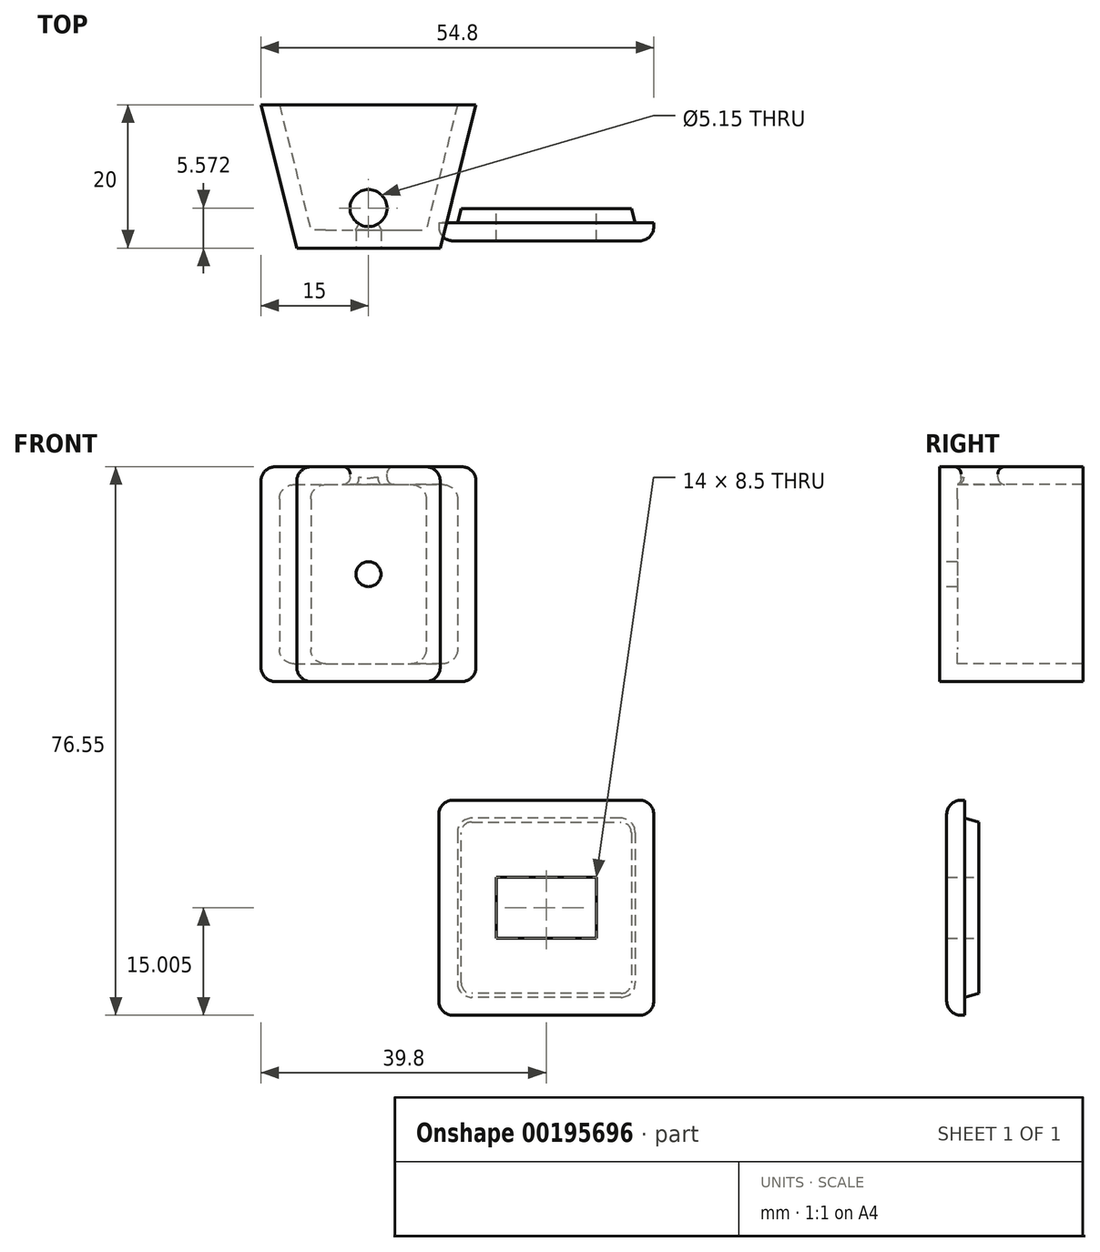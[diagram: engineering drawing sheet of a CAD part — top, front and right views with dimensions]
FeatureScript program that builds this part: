
annotation { "Feature Type Name" : "Feature", "Feature Type Description" : "" }
export const myFeature = defineFeature(function(context is Context, id is Id, definition is map)
    precondition{}
    {
        {
            var Q0;
            Q0=qCreatedBy(makeId("Top.planeOp"),FACE);
            var sketch = newSketch(context, id + "F0", { "sketchPlane" : qUnion([Q0])});
            skLineSegment(sketch, "E0.bottom", {"start": v(-10, 10) * mm, "end": v(10, 10) * mm});
            skLineSegment(sketch, "E0.top", {"start": v(-10, -10) * mm, "end": v(10, -10) * mm});
            skLineSegment(sketch, "E1", {"start": v(-15, 10) * mm, "end": v(15, 10) * mm});
            skLineSegment(sketch, "E2", {"start": v(15, 10) * mm, "end": v(10, -10) * mm});
            skLineSegment(sketch, "E3", {"start": v(-15, 10) * mm, "end": v(-10, -10) * mm});
            skSolve(sketch);
        }
        {
            var Q0;
            Q0=makeQuery(id+"F0.imprint","IMPRINT",FACE,{"disambiguationData":[TD([[makeQuery(id+"F0.imprint","IMPRINT",EDGE,{"derivedFrom":sQuery(id+"F0.wireOp",EDGE,"E0.top")}),1.0]])]});
            extrude(context, id + "F1", {"entities" : qUnion([Q0]), "depth" : 30 * mm});
        }
        {
            var Q0;
            Q0=makeQuery(id+"F1.opExtrude","SWEPT_FACE",FACE,{"disambiguationData":[OSD([sQuery(id+"F0.wireOp",EDGE,"E1")])]});
            shell(context, id + "F2", {"entities" : qUnion([Q0]), "thickness" : 2.5 * mm});
        }
        {
            var Q0;
            Q0=makeQuery(id+"F1.opExtrude","CAP_EDGE",EDGE,{"disambiguationData":[OSD([sQuery(id+"F0.wireOp",EDGE,"E3")])],"isStart":true});
            var Q1;
            Q1=makeQuery(id+"F1.opExtrude","CAP_EDGE",EDGE,{"disambiguationData":[OSD([sQuery(id+"F0.wireOp",EDGE,"E3")])],"isStart":false});
            var Q2;
            Q2=makeQuery(id+"F1.opExtrude","CAP_EDGE",EDGE,{"disambiguationData":[OSD([sQuery(id+"F0.wireOp",EDGE,"E2")])],"isStart":false});
            var Q3;
            Q3=makeQuery(id+"F1.opExtrude","CAP_EDGE",EDGE,{"disambiguationData":[OSD([sQuery(id+"F0.wireOp",EDGE,"E2")])],"isStart":true});
            var Q4;
            {var subQ0=sQuery(id+"F0.wireOp",EDGE,"E3");Q4=makeQuery(id+"F2.opShell","OFFSET_EDGE",EDGE,{"disambiguationData":[OSD([subQ0]),TDD([makeQuery(id+"F1.opExtrude","CAP_EDGE",EDGE,{"disambiguationData":[OSD([subQ0])],"isStart":false})])]});}
            var Q5;
            {var subQ0=sQuery(id+"F0.wireOp",EDGE,"E2");Q5=makeQuery(id+"F2.opShell","OFFSET_EDGE",EDGE,{"disambiguationData":[OSD([subQ0]),TDD([makeQuery(id+"F1.opExtrude","CAP_EDGE",EDGE,{"disambiguationData":[OSD([subQ0])],"isStart":false})])]});}
            var Q6;
            {var subQ0=sQuery(id+"F0.wireOp",EDGE,"E2");Q6=makeQuery(id+"F2.opShell","OFFSET_EDGE",EDGE,{"disambiguationData":[OSD([subQ0]),TDD([makeQuery(id+"F1.opExtrude","CAP_EDGE",EDGE,{"disambiguationData":[OSD([subQ0])],"isStart":true})])]});}
            var Q7;
            {var subQ0=sQuery(id+"F0.wireOp",EDGE,"E3");Q7=makeQuery(id+"F2.opShell","OFFSET_EDGE",EDGE,{"disambiguationData":[OSD([subQ0]),TDD([makeQuery(id+"F1.opExtrude","CAP_EDGE",EDGE,{"disambiguationData":[OSD([subQ0])],"isStart":true})])]});}
            fillet(context, id + "F3", {"entities" : qUnion([Q0, Q1, Q2, Q3, Q4, Q5, Q6, Q7]), "radius" : 2 * mm, "tangentPropagation" : true, "allowEdgeOverflow" : false});
        }
        {
            var Q0;
            Q0=qCreatedBy(makeId("Front.planeOp"),FACE);
            var sketch = newSketch(context, id + "F4", { "sketchPlane" : qUnion([Q0])});
            skLineSegment(sketch, "E4.bottom", {"start": v(15, -46.55) * mm, "end": v(-15, -46.55) * mm});
            skLineSegment(sketch, "E4.top", {"start": v(15, -16.55) * mm, "end": v(-15, -16.55) * mm});
            skLineSegment(sketch, "E4.left", {"start": v(15, -46.55) * mm, "end": v(15, -16.55) * mm});
            skLineSegment(sketch, "E4.right", {"start": v(-15, -46.55) * mm, "end": v(-15, -16.55) * mm});
            skLineSegment(sketch, "E5.bottom", {"start": v(12.4, -44.05) * mm, "end": v(-12.4, -44.05) * mm});
            skLineSegment(sketch, "E5.top", {"start": v(12.4, -19.05) * mm, "end": v(-12.4, -19.05) * mm});
            skLineSegment(sketch, "E5.left", {"start": v(12.4, -44.05) * mm, "end": v(12.4, -19.05) * mm});
            skLineSegment(sketch, "E5.right", {"start": v(-12.4, -44.05) * mm, "end": v(-12.4, -19.05) * mm});
            skSolve(sketch);
        }
        {
            var Q0;
            Q0=makeQuery(id+"F4.imprint","IMPRINT",FACE,{"disambiguationData":[TD([[makeQuery(id+"F4.imprint","IMPRINT",EDGE,{"derivedFrom":sQuery(id+"F4.wireOp",EDGE,"E4.bottom")}),-1.0]])]});
            var Q1;
            Q1=makeQuery(id+"F4.imprint","IMPRINT",FACE,{"disambiguationData":[TD([[makeQuery(id+"F4.imprint","IMPRINT",EDGE,{"derivedFrom":sQuery(id+"F4.wireOp",EDGE,"E5.bottom")}),-1.0]])]});
            extrude(context, id + "F5", {"entities" : qUnion([Q0, Q1]), "depth" : 2.5 * mm});
        }
        {
            var Q0;
            Q0=makeQuery(id+"F4.imprint","IMPRINT",FACE,{"disambiguationData":[TD([[makeQuery(id+"F4.imprint","IMPRINT",EDGE,{"derivedFrom":sQuery(id+"F4.wireOp",EDGE,"E5.bottom")}),-1.0]])]});
            extrude(context, id + "F6", {"entities" : qUnion([Q0]), "operationType" : NewBodyOperationType.ADD, "depth" : 4.5 * mm});
        }
        {
            var Q0;
            Q0=makeQuery(id+"F5.opExtrude","SWEPT_EDGE",EDGE,{"disambiguationData":[OSD([sQuery(id+"F4.wireOp",EDGE,"E4.bottom"),sQuery(id+"F4.wireOp",EDGE,"E4.left")])]});
            var Q1;
            Q1=makeQuery(id+"F6.opExtrude","SWEPT_EDGE",EDGE,{"disambiguationData":[OSD([sQuery(id+"F4.wireOp",EDGE,"E5.bottom"),sQuery(id+"F4.wireOp",EDGE,"E5.left")])]});
            var Q2;
            Q2=makeQuery(id+"F5.opExtrude","SWEPT_EDGE",EDGE,{"disambiguationData":[OSD([sQuery(id+"F4.wireOp",EDGE,"E4.top"),sQuery(id+"F4.wireOp",EDGE,"E4.left")])]});
            var Q3;
            Q3=makeQuery(id+"F6.opExtrude","SWEPT_EDGE",EDGE,{"disambiguationData":[OSD([sQuery(id+"F4.wireOp",EDGE,"E5.top"),sQuery(id+"F4.wireOp",EDGE,"E5.left")])]});
            var Q4;
            Q4=makeQuery(id+"F5.opExtrude","SWEPT_EDGE",EDGE,{"disambiguationData":[OSD([sQuery(id+"F4.wireOp",EDGE,"E4.bottom"),sQuery(id+"F4.wireOp",EDGE,"E4.right")])]});
            var Q5;
            Q5=makeQuery(id+"F6.opExtrude","SWEPT_EDGE",EDGE,{"disambiguationData":[OSD([sQuery(id+"F4.wireOp",EDGE,"E5.bottom"),sQuery(id+"F4.wireOp",EDGE,"E5.right")])]});
            var Q6;
            Q6=makeQuery(id+"F6.opExtrude","SWEPT_EDGE",EDGE,{"disambiguationData":[OSD([sQuery(id+"F4.wireOp",EDGE,"E5.top"),sQuery(id+"F4.wireOp",EDGE,"E5.right")])]});
            var Q7;
            Q7=makeQuery(id+"F5.opExtrude","SWEPT_EDGE",EDGE,{"disambiguationData":[OSD([sQuery(id+"F4.wireOp",EDGE,"E4.top"),sQuery(id+"F4.wireOp",EDGE,"E4.right")])]});
            fillet(context, id + "F7", {"entities" : qUnion([Q0, Q1, Q2, Q3, Q4, Q5, Q6, Q7]), "radius" : 2 * mm, "tangentPropagation" : true, "allowEdgeOverflow" : false});
        }
        {
            var Q0;
            Q0=makeQuery(id+"F5.opExtrude","CAP_FACE",FACE,{"disambiguationData":[OSD([sQuery(id+"F4.wireOp",EDGE,"E4.bottom"),sQuery(id+"F4.wireOp",EDGE,"E4.top"),sQuery(id+"F4.wireOp",EDGE,"E4.left"),sQuery(id+"F4.wireOp",EDGE,"E4.right")])],"isStart":true});
            fillet(context, id + "F8", {"entities" : qUnion([Q0]), "radius" : 2 * mm, "tangentPropagation" : true, "allowEdgeOverflow" : false});
        }
        {
            var Q0;
            Q0=makeQuery(id+"F5.opExtrude","SWEPT_BODY",BODY,{"disambiguationData":[OSD([sQuery(id+"F4.wireOp",EDGE,"E4.bottom"),sQuery(id+"F4.wireOp",EDGE,"E4.top"),sQuery(id+"F4.wireOp",EDGE,"E4.left"),sQuery(id+"F4.wireOp",EDGE,"E4.right")])]});
            var Q1;
            Q1=makeQuery(id+"F6.opExtrude","CAP_EDGE",EDGE,{"disambiguationData":[OSD([sQuery(id+"F4.wireOp",EDGE,"E5.left")])],"isStart":false});
            transform(context, id + "F9", {"entities" : qUnion([Q0]), "transformType" : TransformType.ROTATION, "transformAxis" : qUnion([Q1]), "angle" : 180 * degree, "makeCopy" : false});
        }
        {
            var Q0;
            Q0=makeQuery(id+"F6.opExtrude","CAP_FACE",FACE,{"disambiguationData":[OSD([sQuery(id+"F4.wireOp",EDGE,"E5.bottom"),sQuery(id+"F4.wireOp",EDGE,"E5.top"),sQuery(id+"F4.wireOp",EDGE,"E5.left"),sQuery(id+"F4.wireOp",EDGE,"E5.right")])],"isStart":false});
            var sketch = newSketch(context, id + "F10", { "sketchPlane" : qUnion([Q0])});
            skLineSegment(sketch, "E6", {"start": v(-24.8, -10.4) * mm, "end": v(-24.8, -54.16) * mm, "construction": true});
            skPoint(sketch, "E6.startSnap0", {"position": v(-24.8, -19.05) * mm});
            skLineSegment(sketch, "E7", {"start": v(-5.09, -31.55) * mm, "end": v(-53.1, -31.55) * mm, "construction": true});
            skPoint(sketch, "E7.startSnap0", {"position": v(-12.4, -31.55) * mm});
            skPoint(sketch, "E7.endSnap0", {"position": v(-37.2, -31.55) * mm});
            skLineSegment(sketch, "E8.bottom", {"start": v(-17.8, -27.3) * mm, "end": v(-31.8, -27.3) * mm});
            skLineSegment(sketch, "E8.top", {"start": v(-17.8, -35.8) * mm, "end": v(-31.8, -35.8) * mm});
            skLineSegment(sketch, "E8.left", {"start": v(-17.8, -27.3) * mm, "end": v(-17.8, -35.8) * mm});
            skLineSegment(sketch, "E8.right", {"start": v(-31.8, -27.3) * mm, "end": v(-31.8, -35.8) * mm});
            skSolve(sketch);
        }
        {
            var Q0;
            Q0 = qSketchRegion(id + "F10", true);
            extrude(context, id + "F11", {"entities" : qUnion([Q0]), "operationType" : NewBodyOperationType.REMOVE, "oppositeDirection" : true, "depth" : 5 * mm});
        }
        {
            var Q0;
            Q0=makeQuery(id+"F1.opExtrude","CAP_FACE",FACE,{"disambiguationData":[OSD([sQuery(id+"F0.wireOp",EDGE,"E0.top"),sQuery(id+"F0.wireOp",EDGE,"E1"),sQuery(id+"F0.wireOp",EDGE,"E2"),sQuery(id+"F0.wireOp",EDGE,"E3")])],"isStart":false});
            var sketch = newSketch(context, id + "F12", { "sketchPlane" : qUnion([Q0])});
            skCircle(sketch, "E9", {"center": v(0, -4.43) * mm, "radius": 2.57 * mm});
            skPoint(sketch, "E9.centerSnap0", {"position": v(-7.28, -4.43) * mm});
            skSolve(sketch);
        }
        {
            var Q0;
            Q0=makeQuery(id+"F12.imprint","IMPRINT",FACE,{"disambiguationData":[TD([[makeQuery(id+"F12.imprint","IMPRINT",EDGE,{"derivedFrom":sQuery(id+"F12.wireOp",EDGE,"E9")}),1.0]])]});
            extrude(context, id + "F13", {"entities" : qUnion([Q0]), "operationType" : NewBodyOperationType.REMOVE, "oppositeDirection" : true, "depth" : 5 * mm});
        }
        {
            var Q0;
            Q0=makeQuery(id+"F13.boolean.opBoolean","COPY",EDGE,{"derivedFrom":makeQuery(id+"F13.opExtrude","CAP_EDGE",EDGE,{"disambiguationData":[OSD([sQuery(id+"F12.wireOp",EDGE,"E9")])],"isStart":true})});
            var Q1;
            Q1=makeQuery(id+"F13.boolean.opBoolean","COPY",FACE,{"derivedFrom":makeQuery(id+"F13.opExtrude","SWEPT_FACE",FACE,{"disambiguationData":[OSD([sQuery(id+"F12.wireOp",EDGE,"E9")])]})});
            fillet(context, id + "F14", {"entities" : qUnion([Q0, Q1]), "radius" : 1 * mm, "tangentPropagation" : true, "allowEdgeOverflow" : false});
        }
        {
            var Q0;
            Q0=makeQuery(id+"F6.opExtrude","CAP_EDGE",EDGE,{"disambiguationData":[OSD([sQuery(id+"F4.wireOp",EDGE,"E5.right")])],"isStart":false});
            var Q1;
            Q1=makeQuery(id+"F6.opExtrude","CAP_EDGE",EDGE,{"disambiguationData":[OSD([sQuery(id+"F4.wireOp",EDGE,"E5.top")])],"isStart":false});
            var Q2;
            Q2=makeQuery(id+"F6.opExtrude","CAP_EDGE",EDGE,{"disambiguationData":[OSD([sQuery(id+"F4.wireOp",EDGE,"E5.left")])],"isStart":false});
            var Q3;
            Q3=makeQuery(id+"F6.opExtrude","CAP_EDGE",EDGE,{"disambiguationData":[OSD([sQuery(id+"F4.wireOp",EDGE,"E5.bottom")])],"isStart":false});
            var Q4;
            {var subQ0=sQuery(id+"F4.wireOp",EDGE,"E5.right");var subQ1=sQuery(id+"F4.wireOp",EDGE,"E5.top");Q4=makeQuery(id+"F7.opFillet","BLEND_EDGE",EDGE,{"blendedFrom":[makeQuery(id+"F6.opExtrude","SWEPT_EDGE",EDGE,{"disambiguationData":[OSD([subQ1,subQ0])]}),makeQuery(id+"F6.opExtrude","CAP_FACE",FACE,{"disambiguationData":[OSD([sQuery(id+"F4.wireOp",EDGE,"E5.bottom"),subQ1,sQuery(id+"F4.wireOp",EDGE,"E5.left"),subQ0])],"isStart":false})],"blendedInto":[makeQuery(id+"F6.opExtrude","CAP_FACE",FACE,{"disambiguationData":[OSD([sQuery(id+"F4.wireOp",EDGE,"E5.bottom"),subQ1,sQuery(id+"F4.wireOp",EDGE,"E5.left"),subQ0])],"isStart":false})]});}
            var Q5;
            {var subQ0=sQuery(id+"F4.wireOp",EDGE,"E5.right");var subQ1=sQuery(id+"F4.wireOp",EDGE,"E5.bottom");Q5=makeQuery(id+"F7.opFillet","BLEND_EDGE",EDGE,{"blendedFrom":[makeQuery(id+"F6.opExtrude","SWEPT_EDGE",EDGE,{"disambiguationData":[OSD([subQ1,subQ0])]}),makeQuery(id+"F6.opExtrude","CAP_FACE",FACE,{"disambiguationData":[OSD([subQ1,sQuery(id+"F4.wireOp",EDGE,"E5.top"),sQuery(id+"F4.wireOp",EDGE,"E5.left"),subQ0])],"isStart":false})],"blendedInto":[makeQuery(id+"F6.opExtrude","CAP_FACE",FACE,{"disambiguationData":[OSD([subQ1,sQuery(id+"F4.wireOp",EDGE,"E5.top"),sQuery(id+"F4.wireOp",EDGE,"E5.left"),subQ0])],"isStart":false})]});}
            var Q6;
            {var subQ0=sQuery(id+"F4.wireOp",EDGE,"E5.left");var subQ1=sQuery(id+"F4.wireOp",EDGE,"E5.top");Q6=makeQuery(id+"F7.opFillet","BLEND_EDGE",EDGE,{"blendedFrom":[makeQuery(id+"F6.opExtrude","SWEPT_EDGE",EDGE,{"disambiguationData":[OSD([subQ1,subQ0])]}),makeQuery(id+"F6.opExtrude","CAP_FACE",FACE,{"disambiguationData":[OSD([sQuery(id+"F4.wireOp",EDGE,"E5.bottom"),subQ1,subQ0,sQuery(id+"F4.wireOp",EDGE,"E5.right")])],"isStart":false})],"blendedInto":[makeQuery(id+"F6.opExtrude","CAP_FACE",FACE,{"disambiguationData":[OSD([sQuery(id+"F4.wireOp",EDGE,"E5.bottom"),subQ1,subQ0,sQuery(id+"F4.wireOp",EDGE,"E5.right")])],"isStart":false})]});}
            var Q7;
            {var subQ0=sQuery(id+"F4.wireOp",EDGE,"E5.left");var subQ1=sQuery(id+"F4.wireOp",EDGE,"E5.bottom");Q7=makeQuery(id+"F7.opFillet","BLEND_EDGE",EDGE,{"blendedFrom":[makeQuery(id+"F6.opExtrude","SWEPT_EDGE",EDGE,{"disambiguationData":[OSD([subQ1,subQ0])]}),makeQuery(id+"F6.opExtrude","CAP_FACE",FACE,{"disambiguationData":[OSD([subQ1,sQuery(id+"F4.wireOp",EDGE,"E5.top"),subQ0,sQuery(id+"F4.wireOp",EDGE,"E5.right")])],"isStart":false})],"blendedInto":[makeQuery(id+"F6.opExtrude","CAP_FACE",FACE,{"disambiguationData":[OSD([subQ1,sQuery(id+"F4.wireOp",EDGE,"E5.top"),subQ0,sQuery(id+"F4.wireOp",EDGE,"E5.right")])],"isStart":false})]});}
            chamfer(context, id + "F15", {"entities" : qUnion([Q0, Q1, Q2, Q3, Q4, Q5, Q6, Q7]), "chamferType" : ChamferType.OFFSET_ANGLE, "width" : 2 * mm, "oppositeDirection" : false, "angle" : 15 * degree});
        }
        {
            var Q0;
            Q0=makeQuery(id+"F1.opExtrude","SWEPT_FACE",FACE,{"disambiguationData":[OSD([sQuery(id+"F0.wireOp",EDGE,"E0.top")])]});
            var sketch = newSketch(context, id + "F16", { "sketchPlane" : qUnion([Q0])});
            skCircle(sketch, "E10", {"center": v(0, 15) * mm, "radius": 1.74 * mm});
            skPoint(sketch, "E10.centerSnap0", {"position": v(-10, 15) * mm});
            skPoint(sketch, "E10.centerSnap1", {"position": v(0, 30) * mm});
            skSolve(sketch);
        }
        {
            var Q0;
            Q0=makeQuery(id+"F16.imprint","IMPRINT",FACE,{"disambiguationData":[TD([[makeQuery(id+"F16.imprint","IMPRINT",EDGE,{"derivedFrom":sQuery(id+"F16.wireOp",EDGE,"E10")}),1.0]])]});
            extrude(context, id + "F17", {"entities" : qUnion([Q0]), "operationType" : NewBodyOperationType.REMOVE, "oppositeDirection" : true, "depth" : 5 * mm});
        }
    });
